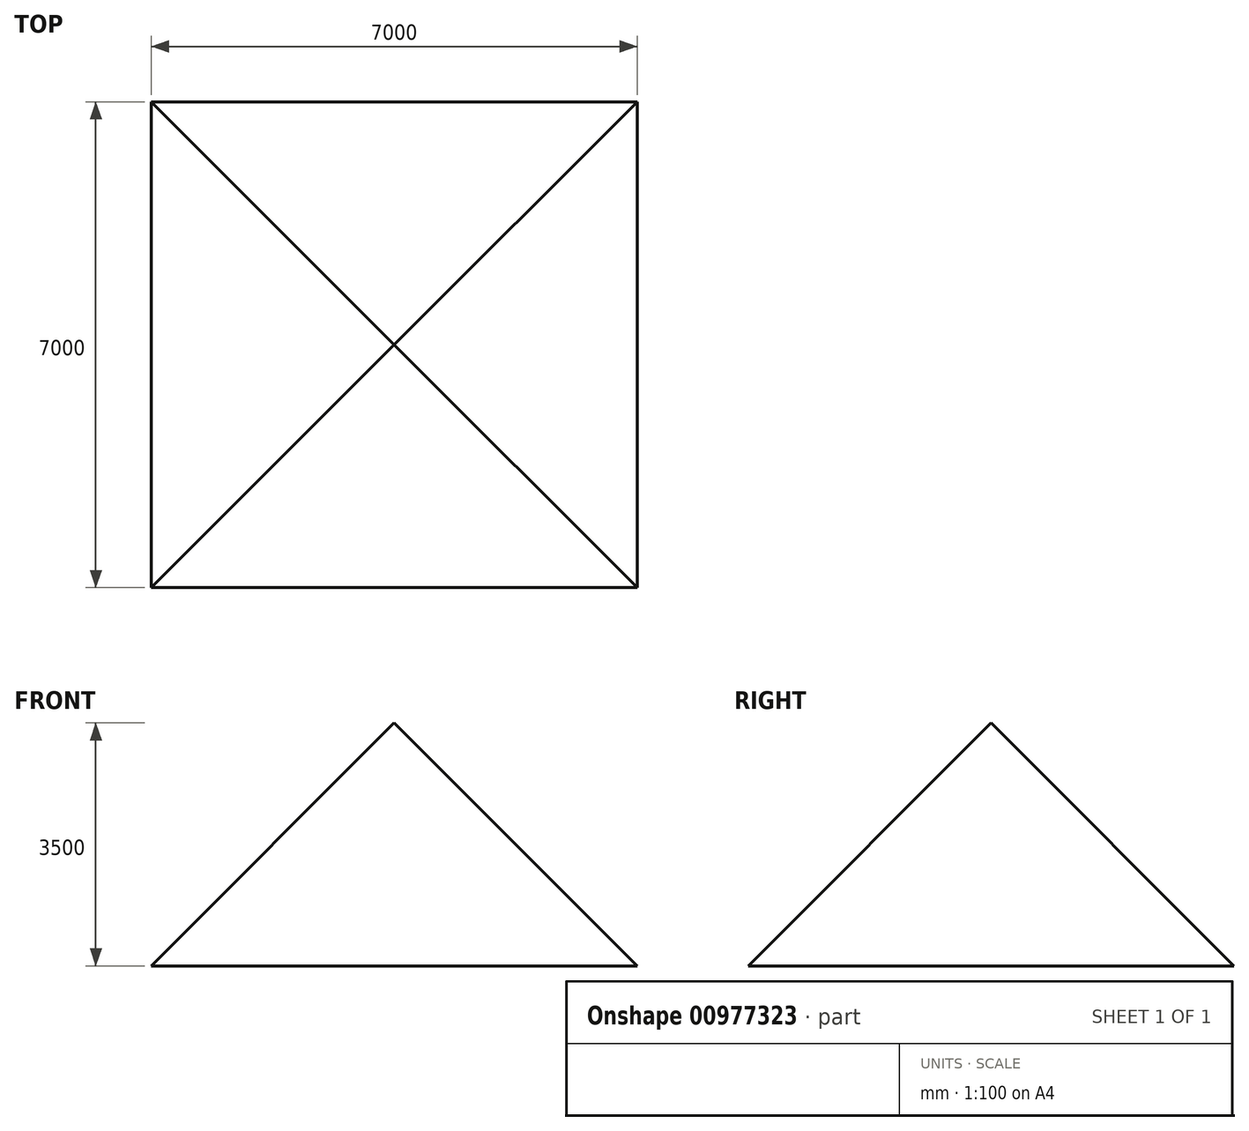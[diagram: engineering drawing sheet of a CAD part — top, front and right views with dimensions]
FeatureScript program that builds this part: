
annotation { "Feature Type Name" : "Feature", "Feature Type Description" : "" }
export const myFeature = defineFeature(function(context is Context, id is Id, definition is map)
    precondition{}
    {
        {
            var Q0;
            Q0=qCreatedBy(makeId("Top.planeOp"),FACE);
            var sketch = newSketch(context, id + "F0", { "sketchPlane" : qUnion([Q0])});
            skLineSegment(sketch, "E0.bottom", {"start": v(0, 0) * mm, "end": v(7000, 0) * mm});
            skLineSegment(sketch, "E0.top", {"start": v(0, 7000) * mm, "end": v(7000, 7000) * mm});
            skLineSegment(sketch, "E0.left", {"start": v(0, 0) * mm, "end": v(0, 7000) * mm});
            skLineSegment(sketch, "E0.right", {"start": v(7000, 0) * mm, "end": v(7000, 7000) * mm});
            skSolve(sketch);
        }
        {
            var Q0;
            Q0 = qSketchRegion(id + "F0", true);
            extrude(context, id + "F1", {"entities" : qUnion([Q0]), "depth" : 7000 * mm, "offsetDistance" : 25 * mm});
        }
        {
            var Q0;
            Q0=makeQuery(id+"F1.opExtrude","CAP_EDGE",EDGE,{"disambiguationData":[OSD([sQuery(id+"F0.wireOp",EDGE,"E0.bottom")])],"isStart":false});
            var Q1;
            Q1=makeQuery(id+"F1.opExtrude","CAP_EDGE",EDGE,{"disambiguationData":[OSD([sQuery(id+"F0.wireOp",EDGE,"E0.right")])],"isStart":false});
            var Q2;
            Q2=makeQuery(id+"F1.opExtrude","CAP_EDGE",EDGE,{"disambiguationData":[OSD([sQuery(id+"F0.wireOp",EDGE,"E0.top")])],"isStart":false});
            var Q3;
            Q3=makeQuery(id+"F1.opExtrude","CAP_EDGE",EDGE,{"disambiguationData":[OSD([sQuery(id+"F0.wireOp",EDGE,"E0.left")])],"isStart":false});
            chamfer(context, id + "F2", {"entities" : qUnion([Q0, Q1, Q2, Q3]), "width" : 3500 * mm, "tangentPropagation" : true});
        }
        {
            var Q0;
            Q0=makeQuery(id+"F1.opExtrude","CAP_FACE",FACE,{"disambiguationData":[OSD([sQuery(id+"F0.wireOp",EDGE,"E0.bottom"),sQuery(id+"F0.wireOp",EDGE,"E0.top"),sQuery(id+"F0.wireOp",EDGE,"E0.left"),sQuery(id+"F0.wireOp",EDGE,"E0.right")])],"isStart":true});
            extrude(context, id + "F3", {"entities" : qUnion([Q0]), "operationType" : NewBodyOperationType.REMOVE, "oppositeDirection" : true, "depth" : 3500 * mm, "offsetDistance" : 25 * mm});
        }
    });
